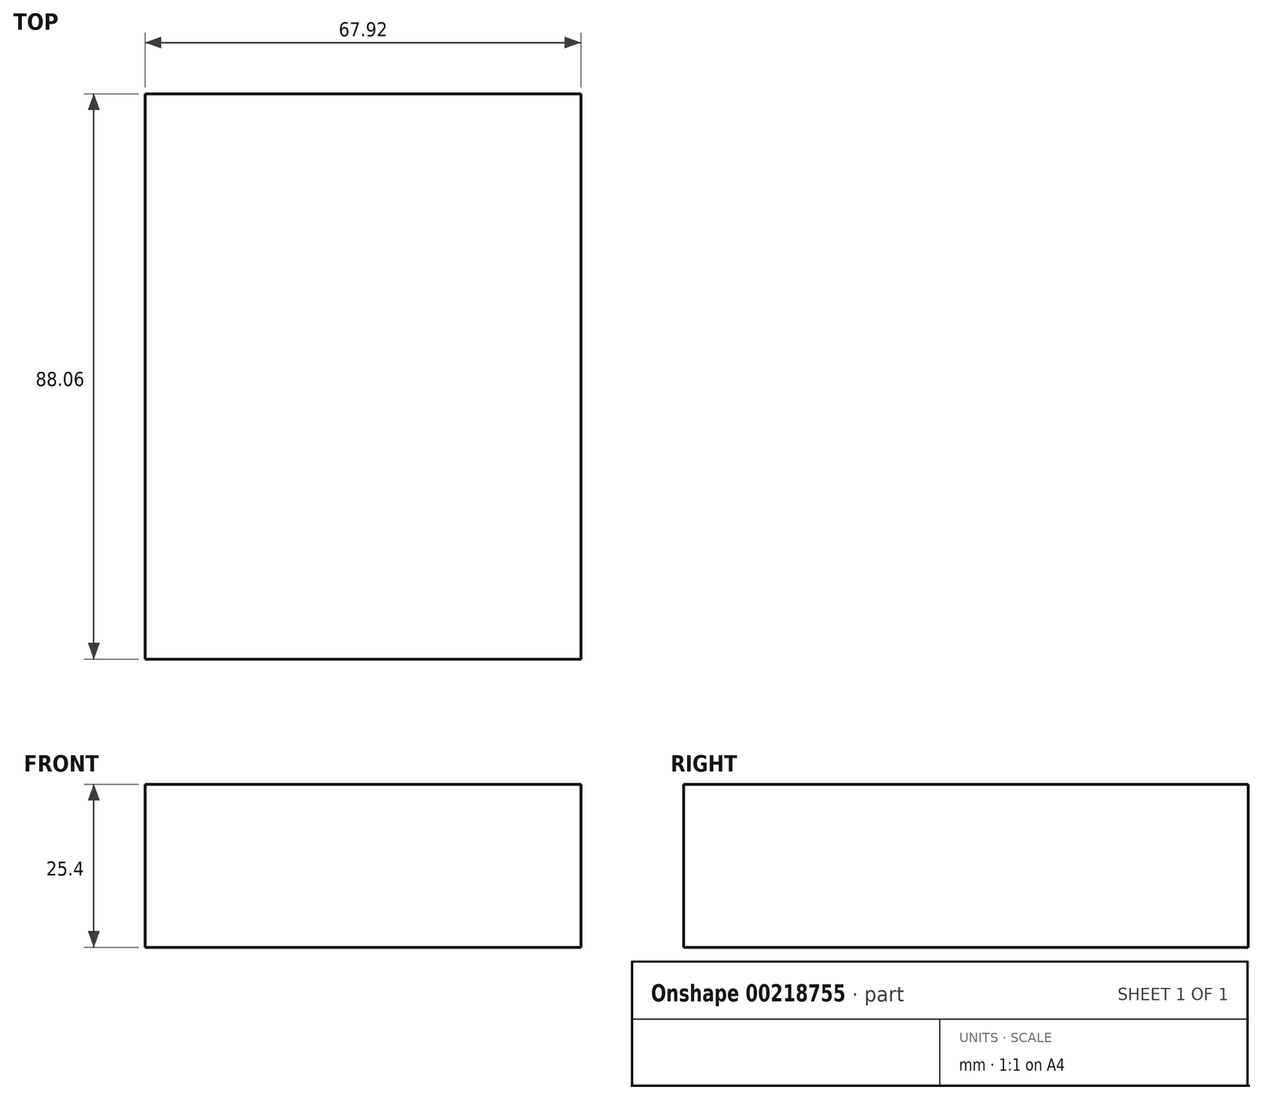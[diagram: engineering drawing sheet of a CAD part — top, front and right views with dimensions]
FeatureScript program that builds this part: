
annotation { "Feature Type Name" : "Feature", "Feature Type Description" : "" }
export const myFeature = defineFeature(function(context is Context, id is Id, definition is map)
    precondition{}
    {
        {
            var Q0;
            Q0=qCreatedBy(makeId("Top.planeOp"),FACE);
            var sketch = newSketch(context, id + "F0", { "sketchPlane" : qUnion([Q0])});
            skLineSegment(sketch, "E0.bottom", {"start": v(33.96, 44.03) * mm, "end": v(-33.96, 44.03) * mm});
            skLineSegment(sketch, "E0.top", {"start": v(33.96, -44.03) * mm, "end": v(-33.96, -44.03) * mm});
            skLineSegment(sketch, "E0.left", {"start": v(33.96, 44.03) * mm, "end": v(33.96, -44.03) * mm});
            skLineSegment(sketch, "E0.right", {"start": v(-33.96, 44.03) * mm, "end": v(-33.96, -44.03) * mm});
            skPoint(sketch, "E0.middle", {"position": v(0, 0) * mm});
            skSolve(sketch);
        }
        {
            var Q0;
            Q0=makeQuery(id+"F0.imprint","IMPRINT",FACE,{"disambiguationData":[TD([[makeQuery(id+"F0.imprint","IMPRINT",EDGE,{"derivedFrom":sQuery(id+"F0.wireOp",EDGE,"E0.bottom")}),1.0]])]});
            extrude(context, id + "F1", {"entities" : qUnion([Q0]), "depth" : 25.4 * mm});
        }
        {
            var Q0;
            Q0=makeQuery(id+"F0.imprint","IMPRINT",FACE,{"disambiguationData":[TD([[makeQuery(id+"F0.imprint","IMPRINT",EDGE,{"derivedFrom":sQuery(id+"F0.wireOp",EDGE,"E0.bottom")}),1.0]])]});
            extrude(context, id + "F2", {"entities" : qUnion([Q0]), "depth" : 25.4 * mm});
        }
    });
